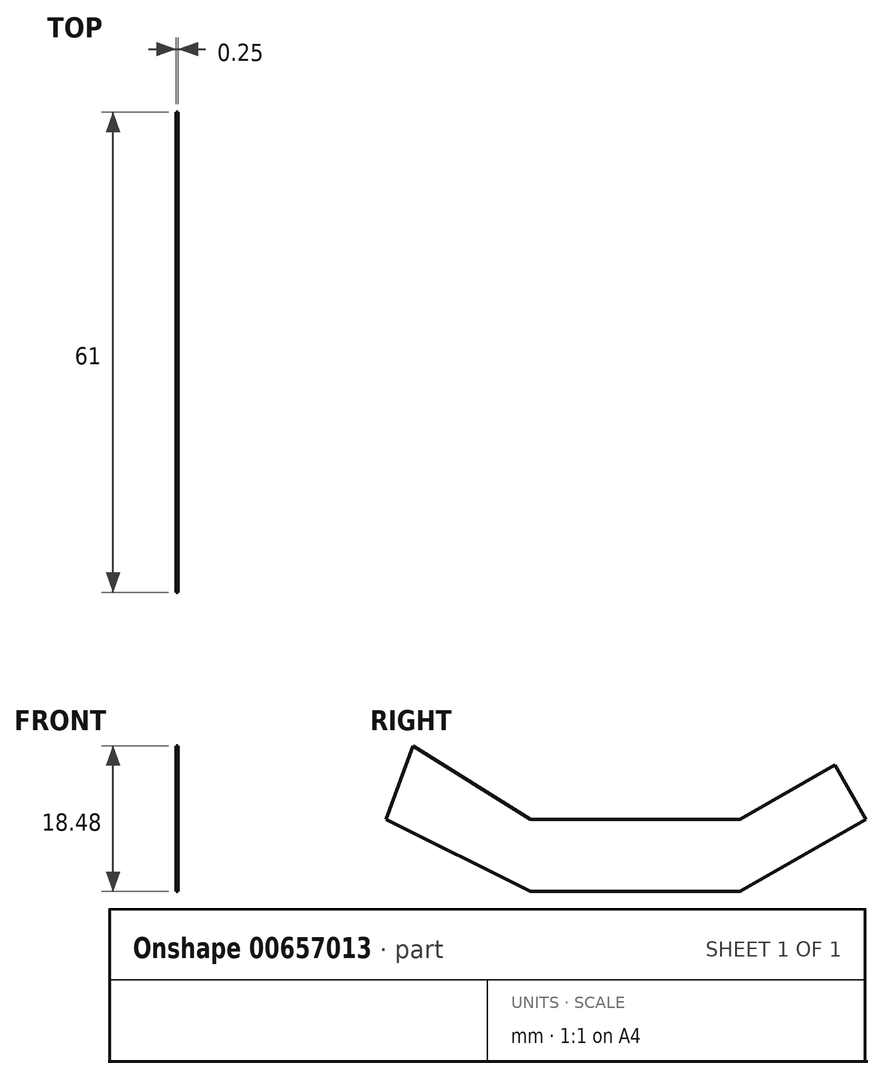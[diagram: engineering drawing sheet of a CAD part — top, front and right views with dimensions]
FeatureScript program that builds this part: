
annotation { "Feature Type Name" : "Feature", "Feature Type Description" : "" }
export const myFeature = defineFeature(function(context is Context, id is Id, definition is map)
    precondition{}
    {
        {
            var Q0;
            Q0=qCreatedBy(makeId("Right.planeOp"),FACE);
            var sketch = newSketch(context, id + "F0", { "sketchPlane" : qUnion([Q0])});
            skLineSegment(sketch, "E0", {"start": v(-132.7, 32.54) * mm, "end": v(-117.77, 23.2) * mm});
            skLineSegment(sketch, "E1", {"start": v(-117.77, 23.2) * mm, "end": v(-91.16, 23.2) * mm});
            skLineSegment(sketch, "E2", {"start": v(-91.16, 23.2) * mm, "end": v(-79.09, 30.1) * mm});
            skLineSegment(sketch, "E3", {"start": v(-79.09, 30.1) * mm, "end": v(-75.15, 23.2) * mm});
            skLineSegment(sketch, "E4", {"start": v(-75.15, 23.2) * mm, "end": v(-91.16, 14.06) * mm});
            skLineSegment(sketch, "E5", {"start": v(-91.16, 14.06) * mm, "end": v(-117.77, 14.06) * mm});
            skLineSegment(sketch, "E6", {"start": v(-117.77, 14.06) * mm, "end": v(-136.15, 23.2) * mm});
            skLineSegment(sketch, "E7", {"start": v(-136.15, 23.2) * mm, "end": v(-132.7, 32.54) * mm});
            skSolve(sketch);
        }
        {
            var Q0;
            Q0=makeQuery(id+"F0.imprint","IMPRINT",FACE,{"disambiguationData":[TD([[makeQuery(id+"F0.imprint","IMPRINT",EDGE,{"derivedFrom":sQuery(id+"F0.wireOp",EDGE,"E0")}),-1.0]])]});
            extrude(context, id + "F1", {"entities" : qUnion([Q0]), "depth" : 0.25 * mm, "offsetDistance" : 25.4 * mm});
        }
    });
